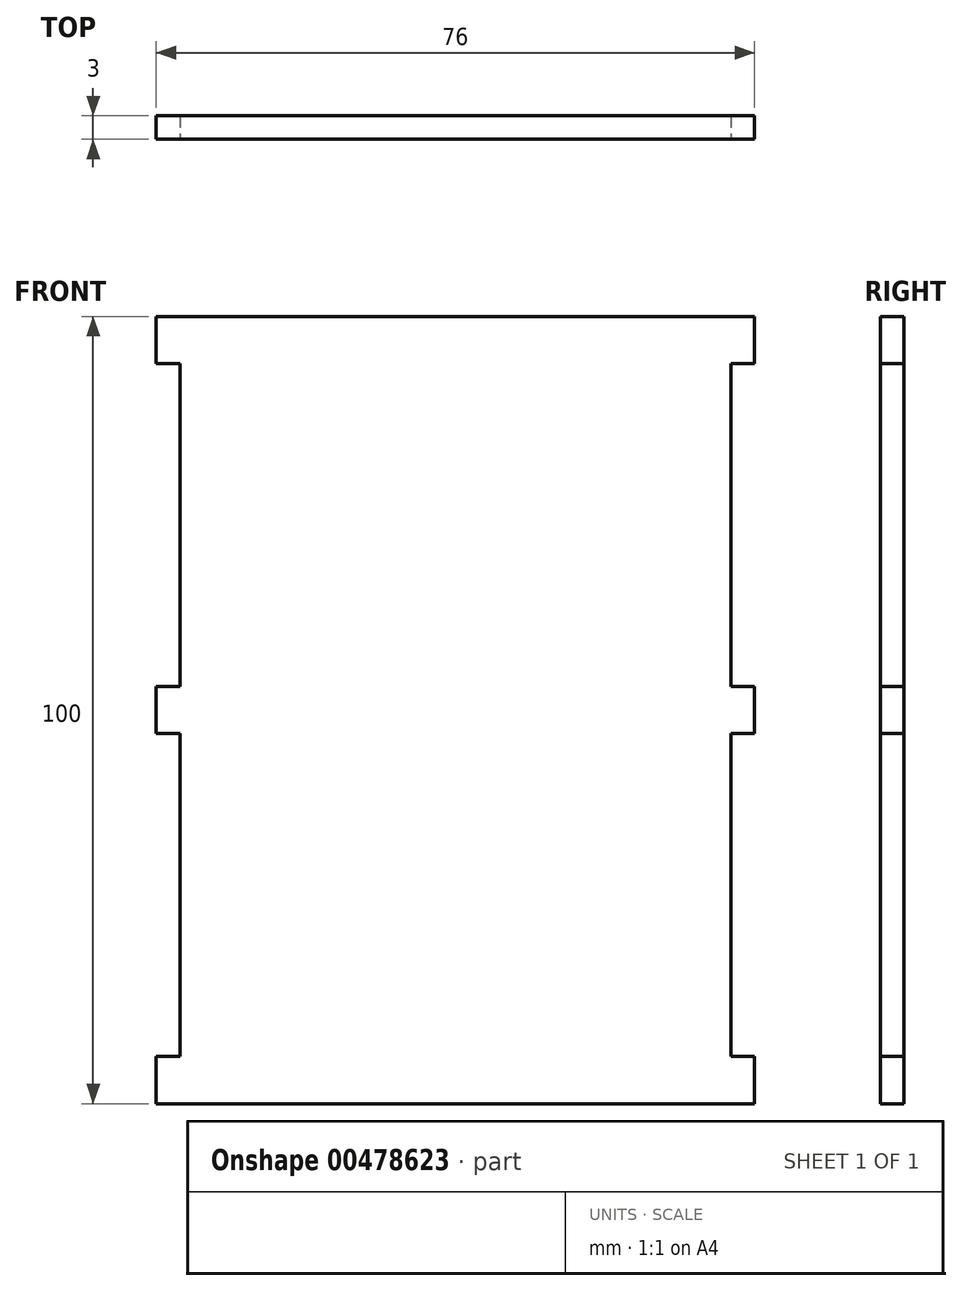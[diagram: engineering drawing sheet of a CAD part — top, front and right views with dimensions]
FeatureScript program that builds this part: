
annotation { "Feature Type Name" : "Feature", "Feature Type Description" : "" }
export const myFeature = defineFeature(function(context is Context, id is Id, definition is map)
    precondition{}
    {
        {
            var Q0;
            Q0=qCreatedBy(makeId("Front.planeOp"),FACE);
            var sketch = newSketch(context, id + "F0", { "sketchPlane" : qUnion([Q0])});
            skLineSegment(sketch, "E0.bottom", {"start": v(35, 50) * mm, "end": v(-35, 50) * mm});
            skLineSegment(sketch, "E0.top", {"start": v(35, -50) * mm, "end": v(-35, -50) * mm});
            skLineSegment(sketch, "E0.left", {"start": v(35, 50) * mm, "end": v(35, -50) * mm});
            skLineSegment(sketch, "E0.right", {"start": v(-35, 50) * mm, "end": v(-35, -50) * mm});
            skPoint(sketch, "E0.middle", {"position": v(0, 0) * mm});
            skSolve(sketch);
        }
        {
            var Q0;
            Q0 = qSketchRegion(id + "F0", true);
            extrude(context, id + "F1", {"entities" : qUnion([Q0]), "depth" : 3 * mm});
        }
        {
            var Q0;
            Q0=makeQuery(id+"F1.opExtrude","CAP_FACE",FACE,{"disambiguationData":[OSD([sQuery(id+"F0.wireOp",EDGE,"E0.bottom"),sQuery(id+"F0.wireOp",EDGE,"E0.top"),sQuery(id+"F0.wireOp",EDGE,"E0.left"),sQuery(id+"F0.wireOp",EDGE,"E0.right")])],"isStart":false});
            var sketch = newSketch(context, id + "F2", { "sketchPlane" : qUnion([Q0])});
            skLineSegment(sketch, "E1.bottom", {"start": v(-35, 50) * mm, "end": v(-38, 50) * mm});
            skLineSegment(sketch, "E1.top", {"start": v(-35, 44) * mm, "end": v(-38, 44) * mm});
            skLineSegment(sketch, "E1.left", {"start": v(-35, 50) * mm, "end": v(-35, 44) * mm});
            skLineSegment(sketch, "E1.right", {"start": v(-38, 50) * mm, "end": v(-38, 44) * mm});
            skLineSegment(sketch, "E2.bottom", {"start": v(-35, -50) * mm, "end": v(-38, -50) * mm});
            skLineSegment(sketch, "E2.top", {"start": v(-35, -44) * mm, "end": v(-38, -44) * mm});
            skLineSegment(sketch, "E2.left", {"start": v(-35, -50) * mm, "end": v(-35, -44) * mm});
            skLineSegment(sketch, "E2.right", {"start": v(-38, -50) * mm, "end": v(-38, -44) * mm});
            skLineSegment(sketch, "E3", {"start": v(-35, 0) * mm, "end": v(-38, 0) * mm, "construction": true});
            skLineSegment(sketch, "E4.bottom", {"start": v(-35, 3) * mm, "end": v(-38, 3) * mm});
            skLineSegment(sketch, "E4.top", {"start": v(-35, -3) * mm, "end": v(-38, -3) * mm});
            skLineSegment(sketch, "E4.left", {"start": v(-35, 3) * mm, "end": v(-35, -3) * mm});
            skLineSegment(sketch, "E4.right", {"start": v(-38, 3) * mm, "end": v(-38, -3) * mm});
            skPoint(sketch, "E4.middle", {"position": v(-36.5, 0) * mm});
            skLineSegment(sketch, "E5", {"start": v(0, 50) * mm, "end": v(0, 0) * mm, "construction": true});
            skLineSegment(sketch, "E6.MirrorCS", {"start": v(38, 3) * mm, "end": v(38, -3) * mm});
            skLineSegment(sketch, "E7.MirrorCS", {"start": v(35, 3) * mm, "end": v(35, -3) * mm});
            skLineSegment(sketch, "E8.MirrorCS", {"start": v(35, -3) * mm, "end": v(38, -3) * mm});
            skLineSegment(sketch, "E9.MirrorCS", {"start": v(35, 0) * mm, "end": v(38, 0) * mm, "construction": true});
            skLineSegment(sketch, "E10.MirrorCS", {"start": v(35, 3) * mm, "end": v(38, 3) * mm});
            skLineSegment(sketch, "E11.MirrorCS", {"start": v(38, -50) * mm, "end": v(38, -44) * mm});
            skLineSegment(sketch, "E12.MirrorCS", {"start": v(35, -44) * mm, "end": v(38, -44) * mm});
            skLineSegment(sketch, "E13.MirrorCS", {"start": v(35, -50) * mm, "end": v(38, -50) * mm});
            skLineSegment(sketch, "E14.MirrorCS", {"start": v(38, 50) * mm, "end": v(38, 44) * mm});
            skLineSegment(sketch, "E15.MirrorCS", {"start": v(35, 50) * mm, "end": v(35, 44) * mm});
            skLineSegment(sketch, "E16.MirrorCS", {"start": v(35, 44) * mm, "end": v(38, 44) * mm});
            skLineSegment(sketch, "E17.MirrorCS", {"start": v(35, 50) * mm, "end": v(38, 50) * mm});
            skLineSegment(sketch, "E18.MirrorCS", {"start": v(35, -50) * mm, "end": v(35, -44) * mm});
            skPoint(sketch, "E19.MirrorP", {"position": v(36.5, 0) * mm});
            skSolve(sketch);
        }
        {
            var Q0;
            Q0 = qSketchRegion(id + "F2", true);
            extrude(context, id + "F3", {"entities" : qUnion([Q0]), "operationType" : NewBodyOperationType.ADD, "oppositeDirection" : true, "depth" : 3 * mm});
        }
    });
